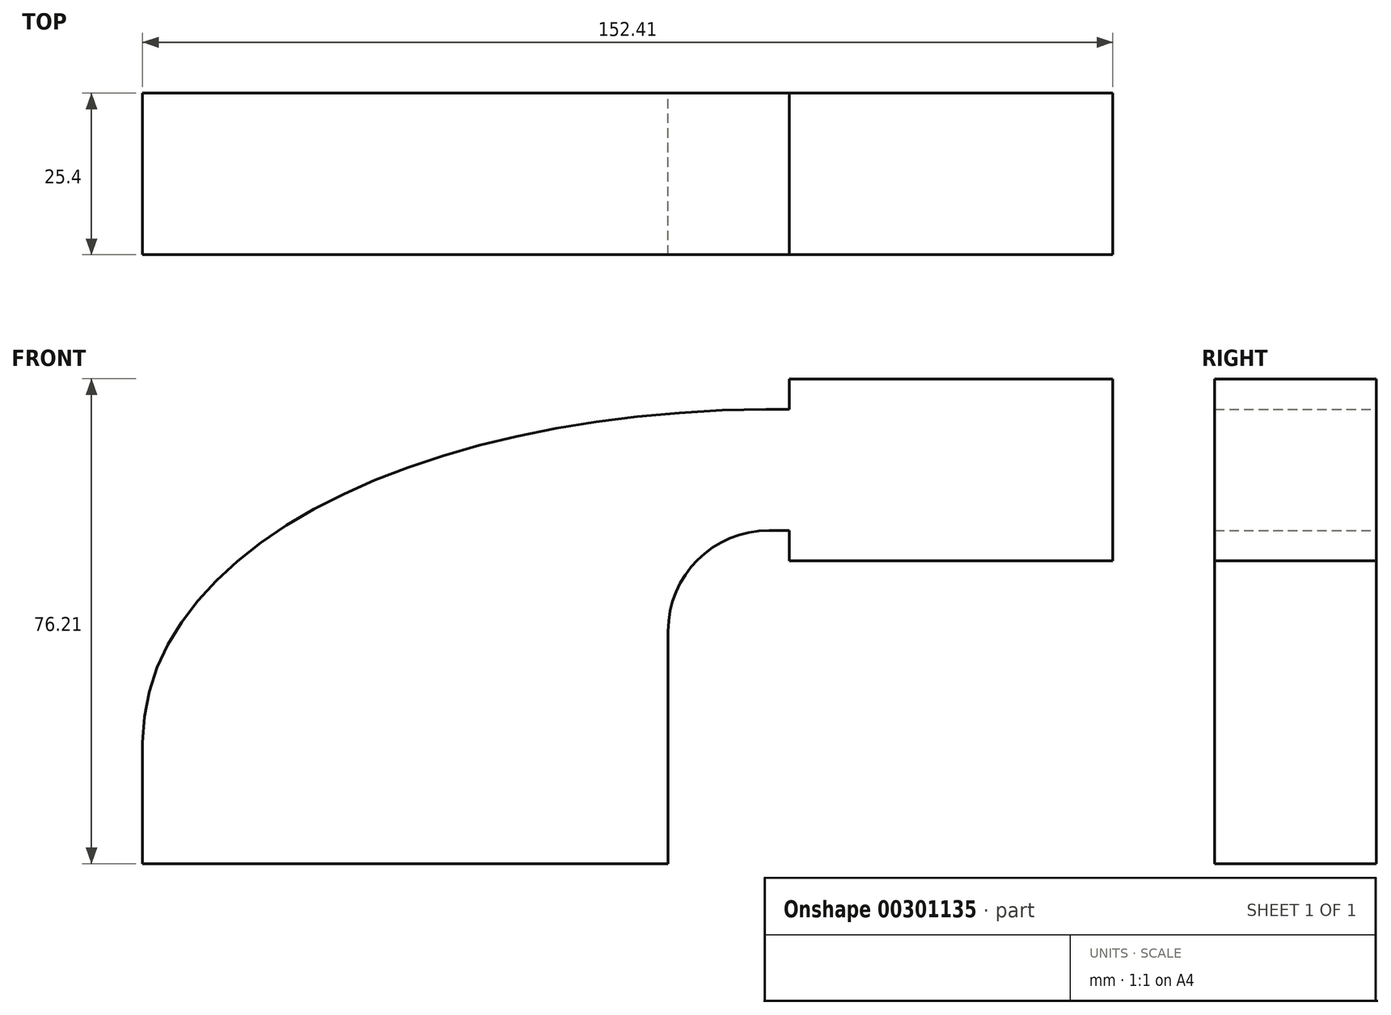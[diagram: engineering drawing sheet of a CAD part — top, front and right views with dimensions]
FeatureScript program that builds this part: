
annotation { "Feature Type Name" : "Feature", "Feature Type Description" : "" }
export const myFeature = defineFeature(function(context is Context, id is Id, definition is map)
    precondition{}
    {
        {
            var Q0;
            Q0=qCreatedBy(makeId("Front.planeOp"),FACE);
            var sketch = newSketch(context, id + "F0", { "sketchPlane" : qUnion([Q0])});
            skLineSegment(sketch, "E0.bottom", {"start": v(41.27, 9.53) * mm, "end": v(-41.28, 9.53) * mm});
            skLineSegment(sketch, "E0.top", {"start": v(41.28, -9.52) * mm, "end": v(-41.27, -9.52) * mm});
            skLineSegment(sketch, "E0.left", {"start": v(41.28, 9.53) * mm, "end": v(41.28, -9.52) * mm});
            skLineSegment(sketch, "E0.right", {"start": v(-41.28, 9.53) * mm, "end": v(-41.27, -9.52) * mm});
            skPoint(sketch, "E0.middle", {"position": v(0, 0) * mm});
            skLineSegment(sketch, "E1.bottom", {"start": v(111.12, 66.68) * mm, "end": v(60.32, 66.68) * mm});
            skLineSegment(sketch, "E1.top", {"start": v(111.12, 38.1) * mm, "end": v(60.32, 38.1) * mm});
            skLineSegment(sketch, "E1.left", {"start": v(111.12, 66.68) * mm, "end": v(111.12, 38.1) * mm});
            skLineSegment(sketch, "E1.right", {"start": v(60.32, 66.68) * mm, "end": v(60.32, 38.1) * mm});
            skLineSegment(sketch, "E2", {"start": v(41.27, 9.53) * mm, "end": v(41.27, 26.99) * mm});
            skArc(sketch, "E3", {"start": v(41.27, 26.99) * mm, "mid": v(45.92, 38.21) * mm, "end": v(57.15, 42.86) * mm});
            skLineSegment(sketch, "E4", {"start": v(57.15, 42.86) * mm, "end": v(85.72, 42.86) * mm});
            skLineSegment(sketch, "E5.0", {"start": v(57.15, 61.91) * mm, "end": v(85.72, 61.91) * mm});
            skArc(sketch, "E5.1", {"start": v(22.23, 26.99) * mm, "mid": v(32.45, 51.68) * mm, "end": v(57.15, 61.91) * mm});
            skLineSegment(sketch, "E5.2", {"start": v(22.22, 9.53) * mm, "end": v(22.22, 26.99) * mm});
            skLineSegment(sketch, "E6", {"start": v(85.72, 66.68) * mm, "end": v(85.72, 38.1) * mm});
            skFitSpline(sketch, "E7", {"points": [v(-41.28, 9.52) * mm, v(57.15, 61.91) * mm], "startDerivative": vector(0.9, 95.05) * mm, "endDerivative": vector(159.38, 1.01) * mm});
            skSolve(sketch);
        }
        {
            var Q0;
            Q0 = qSketchRegion(id + "F0", true);
            extrude(context, id + "F1", {"entities" : qUnion([Q0]), "endBound" : BoundingType.SYMMETRIC, "depth" : 25.4 * mm});
        }
    });
